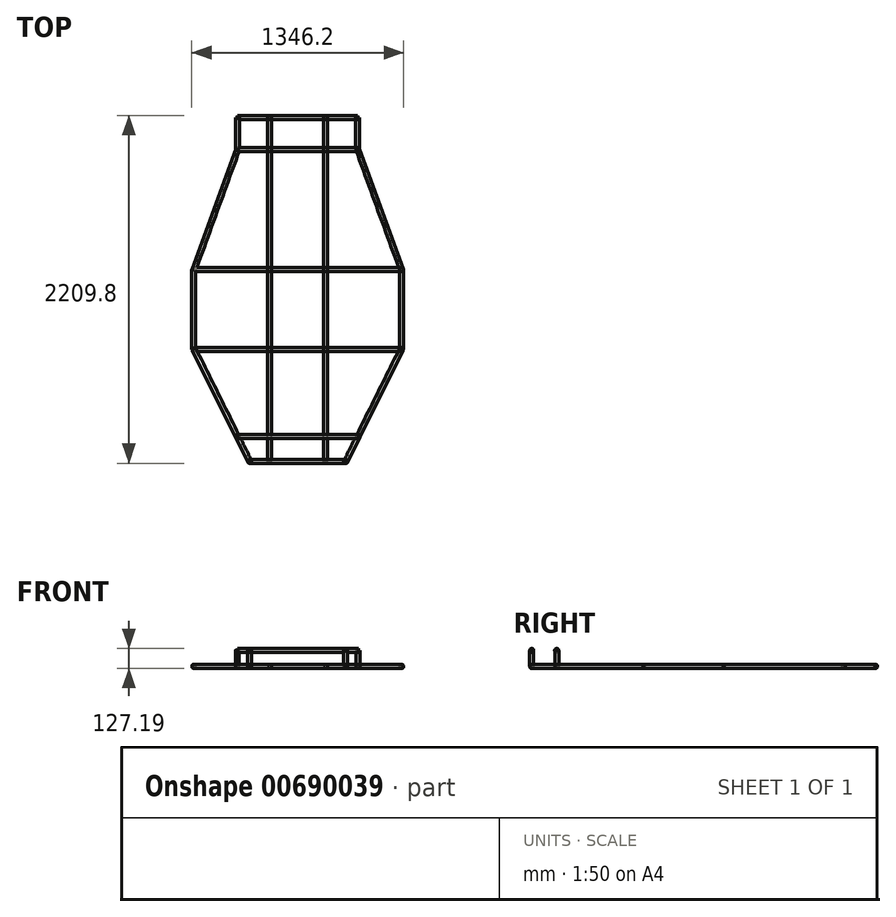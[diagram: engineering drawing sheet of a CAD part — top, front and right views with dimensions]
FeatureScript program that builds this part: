
annotation { "Feature Type Name" : "Feature", "Feature Type Description" : "" }
export const myFeature = defineFeature(function(context is Context, id is Id, definition is map)
    precondition{}
    {
        {
            var Q0;
            Q0=qCreatedBy(makeId("Top.planeOp"),FACE);
            var sketch = newSketch(context, id + "F0", { "sketchPlane" : qUnion([Q0])});
            skLineSegment(sketch, "E0.bottom", {"start": v(381, -101.6) * mm, "end": v(-381, -101.6) * mm});
            skLineSegment(sketch, "E0.top", {"start": v(381, 101.6) * mm, "end": v(-381, 101.6) * mm});
            skLineSegment(sketch, "E0.left", {"start": v(381, -101.6) * mm, "end": v(381, 101.6) * mm});
            skLineSegment(sketch, "E0.right", {"start": v(-381, -101.6) * mm, "end": v(-381, 101.6) * mm});
            skPoint(sketch, "E0.middle", {"position": v(0, 0) * mm});
            skLineSegment(sketch, "E1", {"start": v(-381, -101.6) * mm, "end": v(-658.35, -863.6) * mm});
            skLineSegment(sketch, "E2", {"start": v(-658.35, -863.6) * mm, "end": v(658.35, -863.6) * mm});
            skLineSegment(sketch, "E3", {"start": v(658.35, -863.6) * mm, "end": v(381, -101.6) * mm});
            skLineSegment(sketch, "E4", {"start": v(0, -101.6) * mm, "end": v(0, -863.6) * mm, "construction": true});
            skLineSegment(sketch, "E5", {"start": v(-658.35, -863.6) * mm, "end": v(-658.35, -1371.6) * mm});
            skLineSegment(sketch, "E6", {"start": v(658.35, -863.6) * mm, "end": v(658.35, -1371.6) * mm});
            skLineSegment(sketch, "E7", {"start": v(0, -1371.6) * mm, "end": v(-254, -1371.6) * mm, "construction": true});
            skLineSegment(sketch, "E8", {"start": v(-254, -1371.6) * mm, "end": v(-254, -1270) * mm});
            skLineSegment(sketch, "E9", {"start": v(0, -1371.6) * mm, "end": v(254, -1371.6) * mm, "construction": true});
            skLineSegment(sketch, "E10", {"start": v(254, -1371.6) * mm, "end": v(254, -1270) * mm});
            skLineSegment(sketch, "E11", {"start": v(0, -863.6) * mm, "end": v(0, -1371.6) * mm, "construction": true});
            skLineSegment(sketch, "E12", {"start": v(-658.35, -1371.6) * mm, "end": v(658.35, -1371.6) * mm});
            skLineSegment(sketch, "E13", {"start": v(-658.35, -1371.6) * mm, "end": v(-304.8, -2082.8) * mm});
            skLineSegment(sketch, "E14", {"start": v(-304.8, -2082.8) * mm, "end": v(304.8, -2082.8) * mm});
            skLineSegment(sketch, "E15", {"start": v(304.8, -2082.8) * mm, "end": v(658.35, -1371.6) * mm});
            skLineSegment(sketch, "E16", {"start": v(0, -2082.8) * mm, "end": v(0, -1371.6) * mm, "construction": true});
            skLineSegment(sketch, "E17", {"start": v(-177.8, -2082.8) * mm, "end": v(-177.8, -1371.6) * mm});
            skLineSegment(sketch, "E18", {"start": v(177.8, -2082.8) * mm, "end": v(177.8, -1371.6) * mm});
            skLineSegment(sketch, "E19", {"start": v(-177.8, -1371.6) * mm, "end": v(-177.8, -863.6) * mm});
            skLineSegment(sketch, "E20", {"start": v(177.8, -1371.6) * mm, "end": v(177.8, -863.6) * mm});
            skLineSegment(sketch, "E21", {"start": v(-177.8, -863.6) * mm, "end": v(-177.8, -101.6) * mm});
            skLineSegment(sketch, "E22", {"start": v(177.8, -863.6) * mm, "end": v(177.8, -101.6) * mm});
            skLineSegment(sketch, "E23", {"start": v(-177.8, -101.6) * mm, "end": v(-177.8, 101.6) * mm});
            skLineSegment(sketch, "E24", {"start": v(177.8, -101.6) * mm, "end": v(177.8, 101.6) * mm});
            skSolve(sketch);
        }
        {
            var Q0;
            Q0=qCreatedBy(makeId("Right.planeOp"),FACE);
            var Q1;
            Q1=sQuery(id+"F0.wireOp",VERTEX,"E0.right.end");
            cPlane(context, id + "F1", {"entities" : qUnion([Q0, Q1]), "cplaneType" : CPlaneType.PLANE_POINT, "offset" : 25.4 * mm, "width" : 152.4 * mm, "height" : 152.4 * mm});
        }
        {
            var Q0;
            Q0=qCreatedBy(id+"F1.planeOp",FACE);
            var sketch = newSketch(context, id + "F2", { "sketchPlane" : qUnion([Q0])});
            skLineSegment(sketch, "E25", {"start": v(0, 0) * mm, "end": v(101.6, 0) * mm});
            skCircle(sketch, "E26", {"center": v(101.6, 0) * mm, "radius": 12.7 * mm});
            skLineSegment(sketch, "E27", {"start": v(0, 0) * mm, "end": v(-101.6, 0) * mm});
            skCircle(sketch, "E28", {"center": v(-101.6, 0) * mm, "radius": 12.7 * mm});
            skSolve(sketch);
        }
        {
            var Q0;
            Q0=makeQuery(id+"F2.imprint","IMPRINT",FACE,{"disambiguationData":[TD([[makeQuery(id+"F2.imprint","IMPRINT",EDGE,{"derivedFrom":sQuery(id+"F2.wireOp",EDGE,"E26")}),1.0]])]});
            var Q1;
            Q1=makeQuery(id+"F2.imprint","IMPRINT",FACE,{"disambiguationData":[TD([[makeQuery(id+"F2.imprint","IMPRINT",EDGE,{"derivedFrom":sQuery(id+"F2.wireOp",EDGE,"E28")}),1.0]])]});
            extrude(context, id + "F3", {"entities" : qUnion([Q0, Q1]), "depth" : 762 * mm, "offsetDistance" : 25.4 * mm});
        }
        {
            var Q0;
            Q0=qCreatedBy(makeId("Right.planeOp"),FACE);
            var Q1;
            Q1=sQuery(id+"F0.wireOp",VERTEX,"E2.start");
            cPlane(context, id + "F4", {"entities" : qUnion([Q0, Q1]), "cplaneType" : CPlaneType.PLANE_POINT, "offset" : 25.4 * mm, "width" : 152.4 * mm, "height" : 152.4 * mm});
        }
        {
            var Q0;
            Q0=qCreatedBy(id+"F4.planeOp",FACE);
            var sketch = newSketch(context, id + "F5", { "sketchPlane" : qUnion([Q0])});
            skLineSegment(sketch, "E29", {"start": v(0, 0) * mm, "end": v(-863.6, 0) * mm});
            skCircle(sketch, "E30", {"center": v(-863.6, 0) * mm, "radius": 12.7 * mm});
            skLineSegment(sketch, "E31", {"start": v(-863.6, 0) * mm, "end": v(-1371.6, 0) * mm});
            skCircle(sketch, "E32", {"center": v(-1371.6, 0) * mm, "radius": 12.7 * mm});
            skSolve(sketch);
        }
        {
            var Q0;
            Q0 = qSketchRegion(id + "F5", true);
            extrude(context, id + "F6", {"entities" : qUnion([Q0]), "depth" : 1316.48 * mm, "offsetDistance" : 25.4 * mm});
        }
        {
            var Q0;
            Q0=qCreatedBy(makeId("Right.planeOp"),FACE);
            var Q1;
            Q1=sQuery(id+"F0.wireOp",VERTEX,"E14.start");
            cPlane(context, id + "F7", {"entities" : qUnion([Q0, Q1]), "cplaneType" : CPlaneType.PLANE_POINT, "offset" : 25.4 * mm, "width" : 152.4 * mm, "height" : 152.4 * mm});
        }
        {
            var Q0;
            Q0=qCreatedBy(id+"F7.planeOp",FACE);
            var sketch = newSketch(context, id + "F8", { "sketchPlane" : qUnion([Q0])});
            skLineSegment(sketch, "E33", {"start": v(0, 0) * mm, "end": v(-2082.8, 0) * mm});
            skCircle(sketch, "E34", {"center": v(-2082.8, 0) * mm, "radius": 12.7 * mm});
            skSolve(sketch);
        }
        {
            var Q0;
            Q0 = qSketchRegion(id + "F8", true);
            extrude(context, id + "F9", {"entities" : qUnion([Q0]), "depth" : 609.6 * mm, "offsetDistance" : 25.4 * mm});
        }
        {
            var Q0;
            Q0=sQuery(id+"F0.wireOp",EDGE,"E0.top");
            cPoint(context, id + "F10", {"entities" : qUnion([Q0]), "parameter" : 0.5});
        }
        {
            var Q0;
            Q0=qCreatedBy(makeId("Front.planeOp"),FACE);
            var Q1;
            Q1 = qCreatedBy(id + "F10" ,VERTEX);
            cPlane(context, id + "F11", {"entities" : qUnion([Q0, Q1]), "cplaneType" : CPlaneType.PLANE_POINT, "offset" : 25.4 * mm, "width" : 152.4 * mm, "height" : 152.4 * mm});
        }
        {
            var Q0;
            Q0=qCreatedBy(id+"F11.planeOp",FACE);
            var sketch = newSketch(context, id + "F12", { "sketchPlane" : qUnion([Q0])});
            skLineSegment(sketch, "E35", {"start": v(0, 0) * mm, "end": v(-177.8, 0) * mm});
            skLineSegment(sketch, "E36", {"start": v(177.8, 0) * mm, "end": v(0, 0) * mm});
            skCircle(sketch, "E37", {"center": v(177.8, 0) * mm, "radius": 12.7 * mm});
            skCircle(sketch, "E38", {"center": v(-177.8, 0) * mm, "radius": 12.7 * mm});
            skSolve(sketch);
        }
        {
            var Q0;
            Q0 = qSketchRegion(id + "F12", true);
            extrude(context, id + "F13", {"entities" : qUnion([Q0]), "depth" : 2184.4 * mm, "offsetDistance" : 25.4 * mm});
        }
        {
            var Q0;
            Q0=qCreatedBy(id+"F11.planeOp",FACE);
            var sketch = newSketch(context, id + "F14", { "sketchPlane" : qUnion([Q0])});
            skLineSegment(sketch, "E39", {"start": v(0, 0) * mm, "end": v(381, 0) * mm});
            skLineSegment(sketch, "E40", {"start": v(0, 0) * mm, "end": v(-381, 0) * mm});
            skCircle(sketch, "E41", {"center": v(381, 0) * mm, "radius": 12.7 * mm});
            skCircle(sketch, "E42", {"center": v(-381, 0) * mm, "radius": 12.7 * mm});
            skSolve(sketch);
        }
        {
            var Q0;
            Q0 = qSketchRegion(id + "F14", true);
            extrude(context, id + "F15", {"entities" : qUnion([Q0]), "depth" : 203.2 * mm, "offsetDistance" : 25.4 * mm});
        }
        {
            var Q0;
            Q0=qCreatedBy(makeId("Front.planeOp"),FACE);
            var Q1;
            Q1=sQuery(id+"F0.wireOp",VERTEX,"E6.start");
            cPlane(context, id + "F16", {"entities" : qUnion([Q0, Q1]), "cplaneType" : CPlaneType.PLANE_POINT, "offset" : 25.4 * mm, "width" : 152.4 * mm, "height" : 152.4 * mm});
        }
        {
            var Q0;
            Q0=qCreatedBy(id+"F16.planeOp",FACE);
            var sketch = newSketch(context, id + "F17", { "sketchPlane" : qUnion([Q0])});
            skLineSegment(sketch, "E43", {"start": v(0, 0) * mm, "end": v(660.4, 0) * mm});
            skLineSegment(sketch, "E44", {"start": v(0, 0) * mm, "end": v(-660.4, 0) * mm});
            skCircle(sketch, "E45", {"center": v(660.4, 0) * mm, "radius": 12.7 * mm});
            skCircle(sketch, "E46", {"center": v(-660.4, 0) * mm, "radius": 12.7 * mm});
            skSolve(sketch);
        }
        {
            var Q0;
            Q0 = qSketchRegion(id + "F17", true);
            extrude(context, id + "F18", {"entities" : qUnion([Q0]), "depth" : 508 * mm, "offsetDistance" : 25.4 * mm});
        }
        {
            var Q0;
            Q0=sQuery(id+"F0.wireOp",EDGE,"E3");
            var Q1;
            Q1=sQuery(id+"F0.wireOp",VERTEX,"E0.bottom.start");
            cPlane(context, id + "F19", {"entities" : qUnion([Q0, Q1]), "cplaneType" : CPlaneType.LINE_POINT, "offset" : 25.4 * mm, "width" : 152.4 * mm, "height" : 152.4 * mm});
        }
        {
            var Q0;
            Q0=qCreatedBy(id+"F19.planeOp",FACE);
            var sketch = newSketch(context, id + "F20", { "sketchPlane" : qUnion([Q0])});
            skLineSegment(sketch, "E47", {"start": v(0, 0) * mm, "end": v(-323.85, 0) * mm});
            skCircle(sketch, "E48", {"center": v(-323.85, 0) * mm, "radius": 12.7 * mm});
            skSolve(sketch);
        }
        {
            var Q0;
            Q0 = qSketchRegion(id + "F20", true);
            extrude(context, id + "F21", {"entities" : qUnion([Q0]), "oppositeDirection" : true, "depth" : 815.34 * mm, "offsetDistance" : 25.4 * mm});
        }
        {
            var Q0;
            Q0=sQuery(id+"F0.wireOp",EDGE,"E1");
            var Q1;
            Q1=sQuery(id+"F0.wireOp",VERTEX,"E1.start");
            cPlane(context, id + "F22", {"entities" : qUnion([Q0, Q1]), "cplaneType" : CPlaneType.LINE_POINT, "offset" : 25.4 * mm, "width" : 152.4 * mm, "height" : 152.4 * mm});
        }
        {
            var Q0;
            Q0=qCreatedBy(id+"F22.planeOp",FACE);
            var sketch = newSketch(context, id + "F23", { "sketchPlane" : qUnion([Q0])});
            skLineSegment(sketch, "E49", {"start": v(0, 0) * mm, "end": v(-323.85, 0) * mm});
            skCircle(sketch, "E50", {"center": v(-323.85, 0) * mm, "radius": 12.7 * mm});
            skSolve(sketch);
        }
        {
            var Q0;
            Q0 = qSketchRegion(id + "F23", true);
            extrude(context, id + "F24", {"entities" : qUnion([Q0]), "depth" : 815.34 * mm, "offsetDistance" : 25.4 * mm});
        }
        {
            var Q0;
            Q0=sQuery(id+"F0.wireOp",EDGE,"E15");
            var Q1;
            Q1=sQuery(id+"F0.wireOp",VERTEX,"E12.end");
            cPlane(context, id + "F25", {"entities" : qUnion([Q0, Q1]), "cplaneType" : CPlaneType.LINE_POINT, "offset" : 25.4 * mm, "width" : 152.4 * mm, "height" : 152.4 * mm});
        }
        {
            var Q0;
            Q0=qCreatedBy(id+"F25.planeOp",FACE);
            var sketch = newSketch(context, id + "F26", { "sketchPlane" : qUnion([Q0])});
            skLineSegment(sketch, "E51", {"start": v(0, 0) * mm, "end": v(-1200.15, 0) * mm});
            skCircle(sketch, "E52", {"center": v(-1200.15, 0) * mm, "radius": 12.7 * mm});
            skSolve(sketch);
        }
        {
            var Q0;
            Q0 = qSketchRegion(id + "F26", true);
            extrude(context, id + "F27", {"entities" : qUnion([Q0]), "oppositeDirection" : true, "depth" : 800.1 * mm, "offsetDistance" : 25.4 * mm});
        }
        {
            var Q0;
            Q0=sQuery(id+"F0.wireOp",VERTEX,"E5.end");
            var Q1;
            Q1=sQuery(id+"F0.wireOp",EDGE,"E13");
            cPlane(context, id + "F28", {"entities" : qUnion([Q0, Q1]), "cplaneType" : CPlaneType.LINE_POINT, "offset" : 25.4 * mm, "width" : 152.4 * mm, "height" : 152.4 * mm});
        }
        {
            var Q0;
            Q0=qCreatedBy(id+"F28.planeOp",FACE);
            var sketch = newSketch(context, id + "F29", { "sketchPlane" : qUnion([Q0])});
            skLineSegment(sketch, "E53", {"start": v(0, 0) * mm, "end": v(-1200.15, 0) * mm});
            skCircle(sketch, "E54", {"center": v(-1200.15, 0) * mm, "radius": 12.7 * mm});
            skSolve(sketch);
        }
        {
            var Q0;
            Q0 = qSketchRegion(id + "F29", true);
            extrude(context, id + "F30", {"entities" : qUnion([Q0]), "depth" : 800.1 * mm, "offsetDistance" : 25.4 * mm});
        }
        {
            var Q0;
            Q0=qCreatedBy(makeId("Top.planeOp"),FACE);
            var sketch = newSketch(context, id + "F31", { "sketchPlane" : qUnion([Q0])});
            skLineSegment(sketch, "E55", {"start": v(0, 0) * mm, "end": v(0, -2082.8) * mm, "construction": true});
            skLineSegment(sketch, "E56", {"start": v(0, -2082.8) * mm, "end": v(304.8, -2082.8) * mm, "construction": true});
            skLineSegment(sketch, "E57", {"start": v(0, -2082.8) * mm, "end": v(-304.8, -2082.8) * mm, "construction": true});
            skCircle(sketch, "E58", {"center": v(-304.8, -2082.8) * mm, "radius": 12.7 * mm});
            skCircle(sketch, "E59", {"center": v(304.8, -2082.8) * mm, "radius": 12.7 * mm});
            skLineSegment(sketch, "E60", {"start": v(-304.8, -2082.8) * mm, "end": v(-384.13, -1923.68) * mm, "construction": true});
            skLineSegment(sketch, "E61", {"start": v(-384.13, -1923.68) * mm, "end": v(384.13, -1923.68) * mm, "construction": true});
            skLineSegment(sketch, "E62", {"start": v(384.13, -1923.68) * mm, "end": v(304.8, -2082.8) * mm, "construction": true});
            skCircle(sketch, "E63", {"center": v(-384.13, -1923.68) * mm, "radius": 12.7 * mm});
            skCircle(sketch, "E64", {"center": v(384.13, -1923.68) * mm, "radius": 12.7 * mm});
            skSolve(sketch);
        }
        {
            var Q0;
            Q0 = qSketchRegion(id + "F31", true);
            extrude(context, id + "F32", {"entities" : qUnion([Q0]), "depth" : 101.6 * mm, "offsetDistance" : 25.4 * mm});
        }
        {
            var Q0;
            Q0=makeQuery(id+"F32.opExtrude","CAP_EDGE",EDGE,{"disambiguationData":[OSD([sQuery(id+"F31.wireOp",EDGE,"E58")])],"isStart":false});
            cPlane(context, id + "F33", {"entities" : qUnion([Q0]), "cplaneType" : CPlaneType.LINE_ANGLE, "offset" : 25.4 * mm, "angle" : 0 * degree, "width" : 152.4 * mm, "height" : 152.4 * mm});
        }
        {
            var Q0;
            Q0=qCreatedBy(id+"F33.planeOp",FACE);
            var sketch = newSketch(context, id + "F34", { "sketchPlane" : qUnion([Q0])});
            skLineSegment(sketch, "E65", {"start": v(0, 0) * mm, "end": v(-2082.8, 0) * mm, "construction": true});
            skLineSegment(sketch, "E66", {"start": v(-2082.8, 0) * mm, "end": v(-2082.8, 101.6) * mm, "construction": true});
            skCircle(sketch, "E67", {"center": v(-2082.8, 101.6) * mm, "radius": 12.7 * mm});
            skSolve(sketch);
        }
        {
            var Q0;
            Q0 = qSketchRegion(id + "F34", true);
            extrude(context, id + "F35", {"entities" : qUnion([Q0]), "depth" : 609.6 * mm, "offsetDistance" : 25.4 * mm});
        }
        {
            var Q0;
            Q0=makeQuery(id+"F32.opExtrude","CAP_EDGE",EDGE,{"disambiguationData":[OSD([sQuery(id+"F31.wireOp",EDGE,"E63")])],"isStart":false});
            cPlane(context, id + "F36", {"entities" : qUnion([Q0]), "cplaneType" : CPlaneType.LINE_ANGLE, "offset" : 25.4 * mm, "angle" : 0 * degree, "width" : 152.4 * mm, "height" : 152.4 * mm});
        }
        {
            var Q0;
            Q0=qCreatedBy(id+"F36.planeOp",FACE);
            var sketch = newSketch(context, id + "F37", { "sketchPlane" : qUnion([Q0])});
            skLineSegment(sketch, "E68", {"start": v(0, 0) * mm, "end": v(-1924.05, 0) * mm, "construction": true});
            skLineSegment(sketch, "E69", {"start": v(-1924.05, 0) * mm, "end": v(-1924.05, 101.6) * mm, "construction": true});
            skCircle(sketch, "E70", {"center": v(-1924.05, 101.6) * mm, "radius": 12.89 * mm});
            skSolve(sketch);
        }
        {
            var Q0;
            Q0 = qSketchRegion(id + "F37", true);
            extrude(context, id + "F38", {"entities" : qUnion([Q0]), "depth" : 768.35 * mm, "offsetDistance" : 25.4 * mm});
        }
    });
